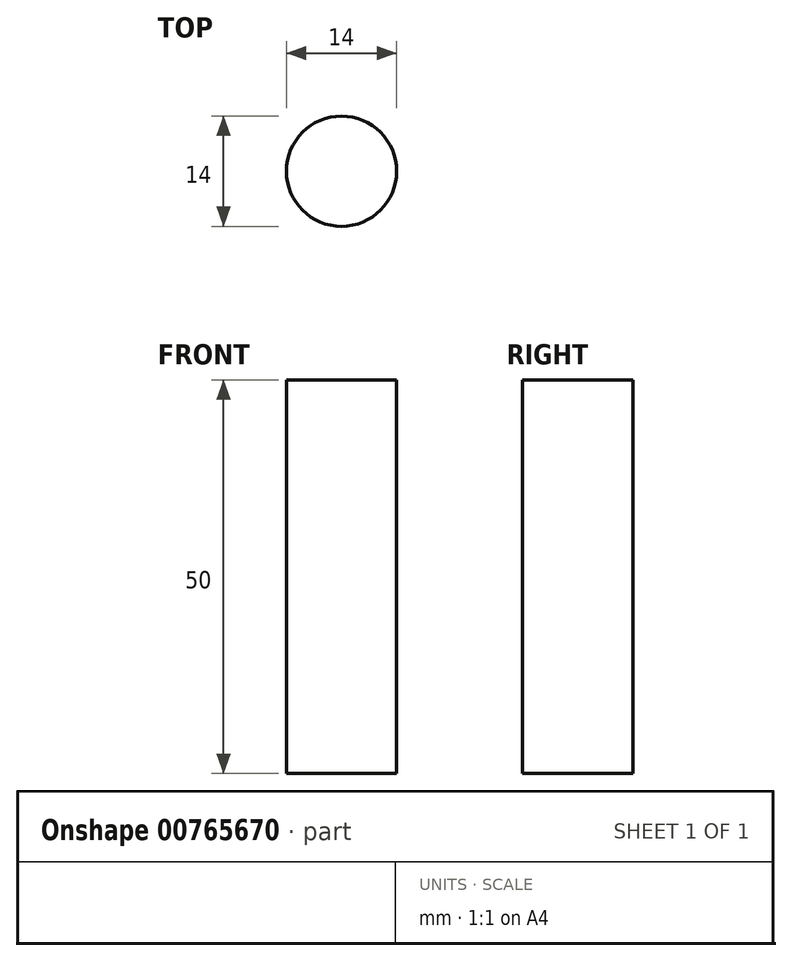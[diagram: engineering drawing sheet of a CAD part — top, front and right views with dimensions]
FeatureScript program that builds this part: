
annotation { "Feature Type Name" : "Feature", "Feature Type Description" : "" }
export const myFeature = defineFeature(function(context is Context, id is Id, definition is map)
    precondition{}
    {
        {
            var Q0;
            Q0=qCreatedBy(makeId("Top.planeOp"),FACE);
            var sketch = newSketch(context, id + "F0", { "sketchPlane" : qUnion([Q0])});
            skCircle(sketch, "E0", {"center": v(0, 0) * mm, "radius": 7 * mm});
            skSolve(sketch);
        }
        {
            var Q0;
            Q0=makeQuery(id+"F0.imprint","IMPRINT",FACE,{"disambiguationData":[TD([[makeQuery(id+"F0.imprint","IMPRINT",EDGE,{"derivedFrom":sQuery(id+"F0.wireOp",EDGE,"E0")}),1.0]])]});
            extrude(context, id + "F1", {"entities" : qUnion([Q0]), "depth" : 50 * mm, "offsetDistance" : 25.4 * mm});
        }
    });
